# Revit family: Single Width Outline
name_source: partatom
category: Furniture
units: mm (PartAtom-declared; Revit-internal decimal feet)

## family parameters
Always vertical = Yes
Cut with Voids When Loaded = No
OmniClass Number = 23.40.20.00
OmniClass Title = General Furniture and Specialties
Room Calculation Point = No
Shared = No
Work Plane-Based = No

## types (2) — shared parameters
AssetType = Fixed
Category = PR_40_30_78_57
Color = Vision Pallete
Depth = 400 mm  [stored 1.31234 ft]
DurationUnit = Years
ExpectedLife = 10
Finish = Powder Coated Steel
Height = 753 mm  [stored 2.47047 ft]
Keynote = PR_40_30_78_57
ManufacturerName = Bisley
ManufacturerURL = www.bisley.com
Material = Steel
Model = Outline
NBSDescription = Office storage
NBSReference = 45-35-80/360
Name = Floor Standing Outline Frames
NominalHeight = 753 mm  [stored 2.47047 ft]
NominalLength = 400 mm  [stored 1.31234 ft]
NominalWidth = 400 mm  [stored 1.31234 ft]
Plinth Height = 50 mm  [stored 0.164042 ft]
ProductInformation = https://www.bisley.com
Revision = 1
Shape = Rectangular
Uniclass2015Code = PR_40_30_78_57
Uniclass2015Title = 78 - Shelves and Storage Units
Uniclass2015Version = V1.1
WarrantyDescription = Standard Bisley Warranty
WarrantyDurationUnit = Year
Width = 400 mm  [stored 1.31234 ft]
zero-valued in all types: Default Elevation

## per-type parameters (varying)
| type | Frame Type | Shelf Type |
| OF08402 | Outline Frames : 800w 2 High | Shelves : Steel Shelf 400w x 400w |
| OF10402 | Outline Frames : 1000w 2 High | Shelves : Steel Shelf 800w units |

note: column(s) folded — value = type name in every type: ModelNumber, ModelReference

note: [stored X ft] marks values corroborated as IEEE doubles in the binary element streams (Revit-internal decimal feet)

## geometry (parser evidence)
native form markers: Sweep x12
no freeform markers — native parametric forms only
